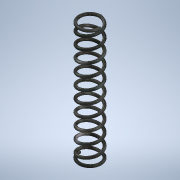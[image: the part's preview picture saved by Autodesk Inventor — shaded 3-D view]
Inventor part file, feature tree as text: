
AUTODESK INVENTOR PART (.ipt)
format: ipt  version: 2020.1 (Build 241239000, 239)  size: 309,760 bytes
history: native  units: mm
features: sketch x3, revolve x2, projected_geometry x2, helix x1
ambient origin geometry x8: Origin, YZ Plane, XZ Plane, XY Plane, X Axis, Y Axis, Z Axis, Center Point
bodies: Solid1 (feature_tree)
feature tree (8):
  helix  "Coil1"  [1 undecoded]
  revolve  "Revolution1"  [1 undecoded]
  revolve  "Revolution2"  Angle=270.0deg
  sketch  "Sketch1"  dims[d1=0.32mm d2=1.2mm]
  sketch  "Sketch2"  dims[d3=1.356mm]
  projected_geometry  "Projected Loop1"
  sketch  "Sketch3"  dims[d4=10.0mm d5=100.0mm d6=0.0mm d7=90.0deg d8=90.0deg d9=0.0mm d10=0.0mm d11=270.0deg d12=270.0deg]
  projected_geometry  "Projected Loop2"
note: 2 required parameter values undecoded (feature->parameter linkage not recoverable at this tier; creation-order binding heuristic only, values carry confidence <= 0.55)